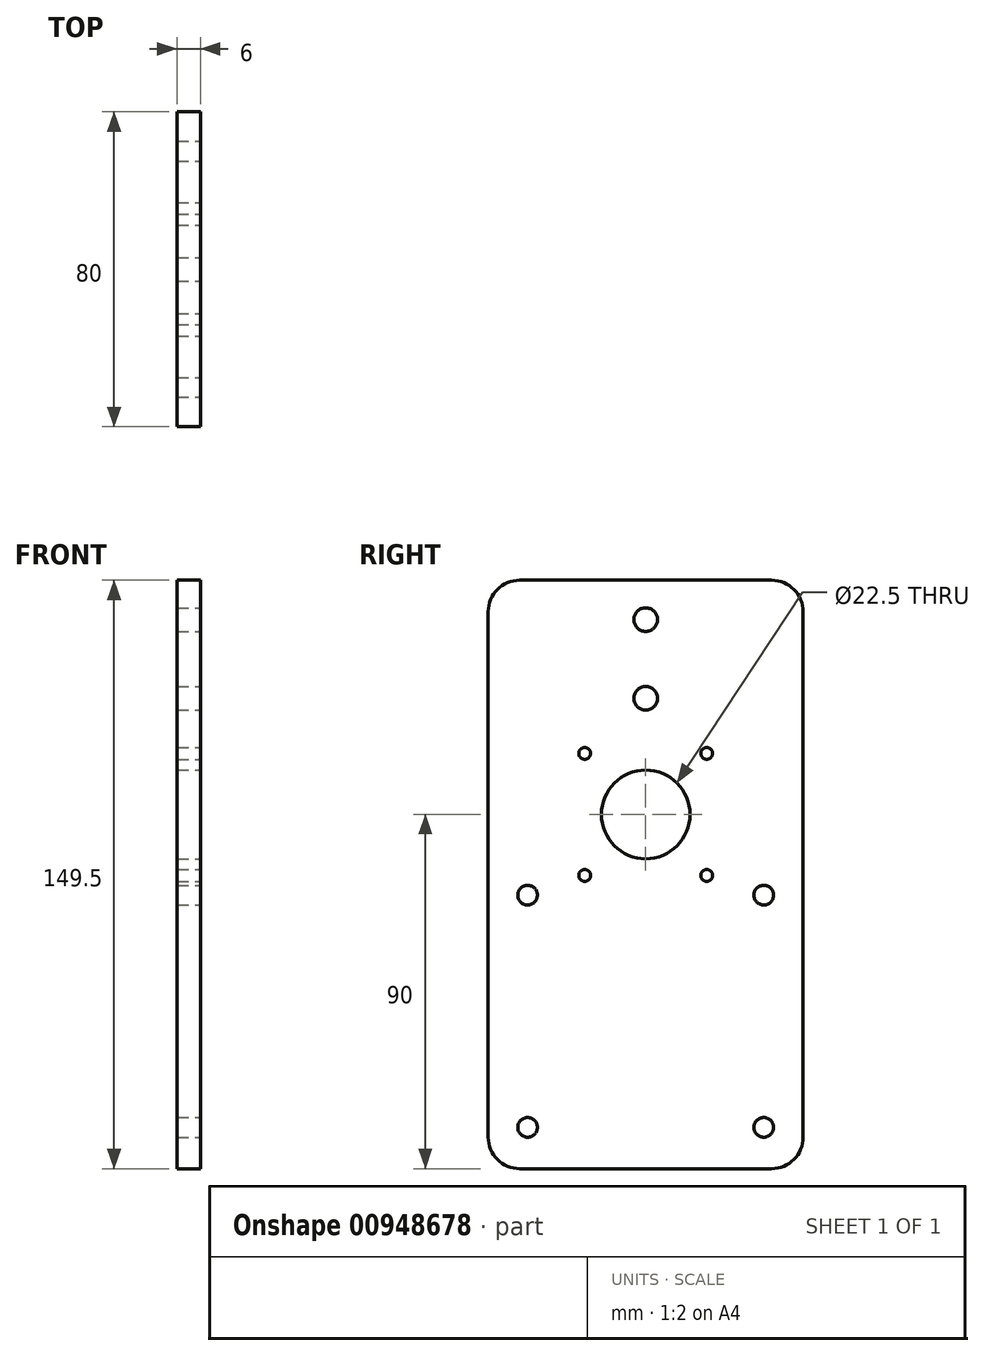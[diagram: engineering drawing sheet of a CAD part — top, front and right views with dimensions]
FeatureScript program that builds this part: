
annotation { "Feature Type Name" : "Feature", "Feature Type Description" : "" }
export const myFeature = defineFeature(function(context is Context, id is Id, definition is map)
    precondition{}
    {
        {
            var Q0;
            Q0=qCreatedBy(makeId("Right.planeOp"),FACE);
            var sketch = newSketch(context, id + "F0", { "sketchPlane" : qUnion([Q0])});
            skLineSegment(sketch, "E0", {"start": v(-28.43, 0) * mm, "end": v(42.81, 0) * mm, "construction": true});
            skLineSegment(sketch, "E1", {"start": v(-28.43, 20) * mm, "end": v(41.92, 20) * mm, "construction": true});
            skLineSegment(sketch, "E2.MirrorCS", {"start": v(-28.43, -20) * mm, "end": v(41.92, -20) * mm, "construction": true});
            skLineSegment(sketch, "E3.bottom", {"start": v(-32, 109.5) * mm, "end": v(32, 109.5) * mm});
            skLineSegment(sketch, "E3.top", {"start": v(-32, -40) * mm, "end": v(32, -40) * mm});
            skLineSegment(sketch, "E3.left", {"start": v(-40, 101.5) * mm, "end": v(-40, -32) * mm});
            skLineSegment(sketch, "E3.right", {"start": v(40, 101.5) * mm, "end": v(40, -32) * mm});
            skPoint(sketch, "E3.middle", {"position": v(0, 0) * mm});
            skCircle(sketch, "E4", {"center": v(-30, 29.5) * mm, "radius": 2.5 * mm});
            skCircle(sketch, "E5.0.1.0", {"center": v(-30, -29.5) * mm, "radius": 2.5 * mm});
            skCircle(sketch, "E5.1.0.0", {"center": v(30, 29.5) * mm, "radius": 2.5 * mm});
            skCircle(sketch, "E5.1.1.0", {"center": v(30, -29.5) * mm, "radius": 2.5 * mm});
            skLineSegment(sketch, "E5.direction1", {"start": v(-30, 29.5) * mm, "end": v(30, 29.5) * mm, "construction": true});
            skLineSegment(sketch, "E5.direction2", {"start": v(-30, 29.5) * mm, "end": v(-30, -29.5) * mm, "construction": true});
            skPoint(sketch, "E6.visualSharp", {"position": v(-40, -40) * mm});
            skArc(sketch, "E6.filletArc", {"start": v(-40, -32) * mm, "mid": v(-37.66, -37.66) * mm, "end": v(-32, -40) * mm});
            skPoint(sketch, "E7.visualSharp", {"position": v(40, -40) * mm});
            skArc(sketch, "E7.filletArc", {"start": v(32, -40) * mm, "mid": v(37.66, -37.66) * mm, "end": v(40, -32) * mm});
            skLineSegment(sketch, "E8", {"start": v(0, 104.35) * mm, "end": v(0, -43.4) * mm, "construction": true});
            skLineSegment(sketch, "E9", {"start": v(-51, 50) * mm, "end": v(59.14, 50) * mm, "construction": true});
            skCircle(sketch, "E10", {"center": v(0, 50) * mm, "radius": 11.25 * mm});
            skCircle(sketch, "E11", {"center": v(-15.5, 65.5) * mm, "radius": 1.5 * mm});
            skCircle(sketch, "E12.0.1.0", {"center": v(-15.5, 34.5) * mm, "radius": 1.5 * mm});
            skCircle(sketch, "E12.1.0.0", {"center": v(15.5, 65.5) * mm, "radius": 1.5 * mm});
            skCircle(sketch, "E12.1.1.0", {"center": v(15.5, 34.5) * mm, "radius": 1.5 * mm});
            skLineSegment(sketch, "E12.direction1", {"start": v(-15.5, 65.5) * mm, "end": v(15.5, 65.5) * mm, "construction": true});
            skLineSegment(sketch, "E12.direction2", {"start": v(-15.5, 65.5) * mm, "end": v(-15.5, 34.5) * mm, "construction": true});
            skCircle(sketch, "E13.0", {"center": v(0, 99.5) * mm, "radius": 3 * mm});
            skCircle(sketch, "E14.0", {"center": v(0, 79.5) * mm, "radius": 3 * mm});
            skLineSegment(sketch, "E15", {"start": v(13.67, 99.5) * mm, "end": v(-17.83, 99.5) * mm, "construction": true});
            skLineSegment(sketch, "E16", {"start": v(14.92, 79.5) * mm, "end": v(-16.92, 79.5) * mm, "construction": true});
            skPoint(sketch, "E17.visualSharp", {"position": v(40, 109.5) * mm});
            skArc(sketch, "E17.filletArc", {"start": v(40, 101.5) * mm, "mid": v(37.66, 107.16) * mm, "end": v(32, 109.5) * mm});
            skPoint(sketch, "E18.visualSharp", {"position": v(-40, 109.5) * mm});
            skArc(sketch, "E18.filletArc", {"start": v(-32, 109.5) * mm, "mid": v(-37.66, 107.16) * mm, "end": v(-40, 101.5) * mm});
            skSolve(sketch);
        }
        {
            var Q0;
            Q0 = qSketchRegion(id + "F0", true);
            extrude(context, id + "F1", {"entities" : qUnion([Q0]), "oppositeDirection" : true, "depth" : 6 * mm, "offsetDistance" : 25 * mm, "symmetric" : true});
        }
    });
